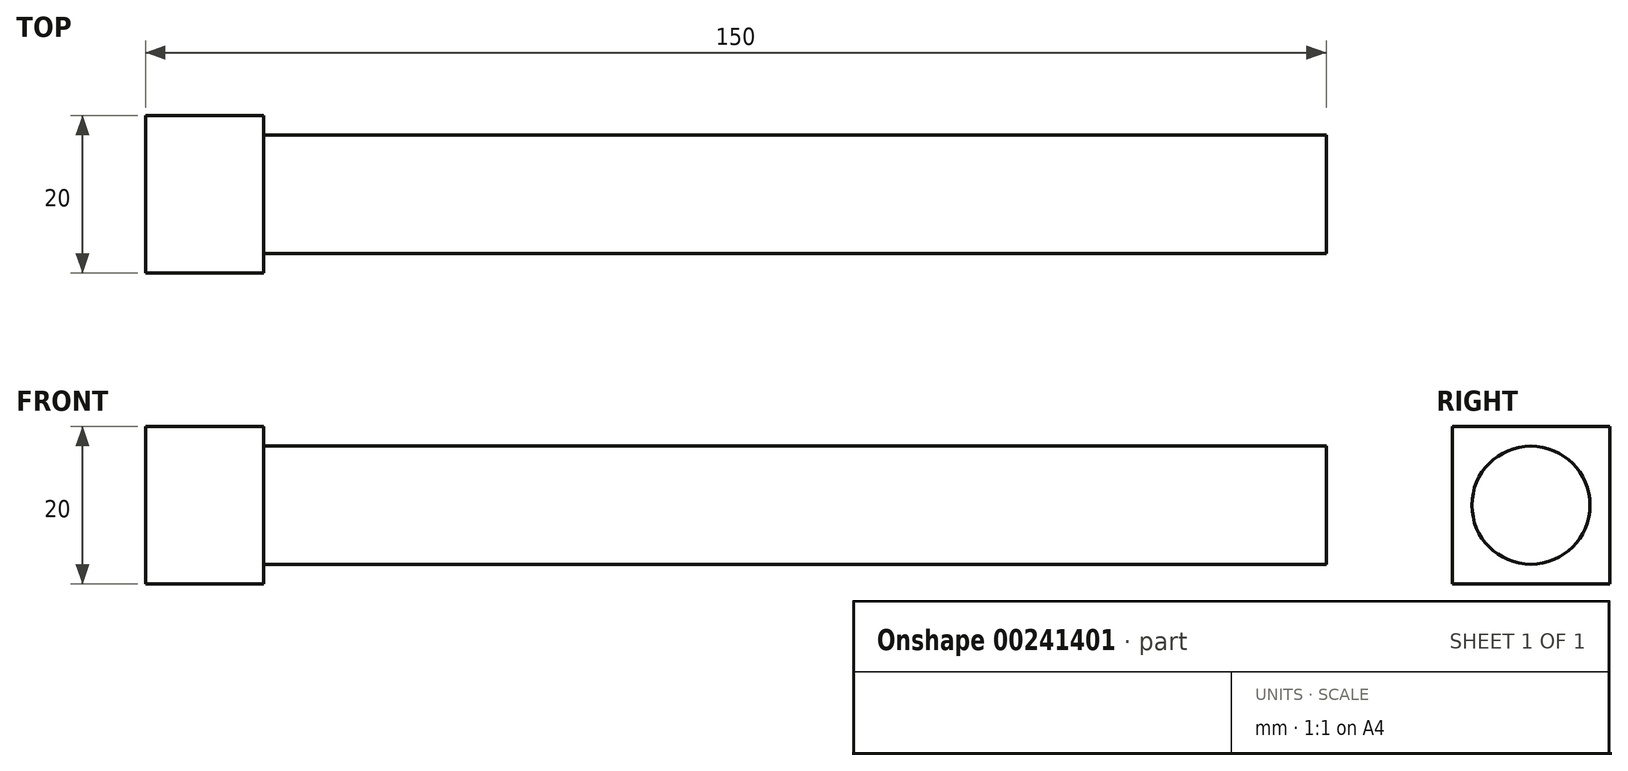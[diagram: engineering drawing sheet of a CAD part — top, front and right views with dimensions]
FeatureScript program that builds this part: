
annotation { "Feature Type Name" : "Feature", "Feature Type Description" : "" }
export const myFeature = defineFeature(function(context is Context, id is Id, definition is map)
    precondition{}
    {
        {
            var Q0;
            Q0=qCreatedBy(makeId("Right.planeOp"),FACE);
            var sketch = newSketch(context, id + "F0", { "sketchPlane" : qUnion([Q0])});
            skLineSegment(sketch, "E0.bottom", {"start": v(-10, 10) * mm, "end": v(10, 10) * mm});
            skLineSegment(sketch, "E0.top", {"start": v(-10, -10) * mm, "end": v(10, -10) * mm});
            skLineSegment(sketch, "E0.left", {"start": v(-10, 10) * mm, "end": v(-10, -10) * mm});
            skLineSegment(sketch, "E0.right", {"start": v(10, 10) * mm, "end": v(10, -10) * mm});
            skPoint(sketch, "E0.middle", {"position": v(0, 0) * mm});
            skSolve(sketch);
        }
        {
            var Q0;
            Q0 = qSketchRegion(id + "F0", true);
            extrude(context, id + "F1", {"entities" : qUnion([Q0]), "depth" : 15 * mm});
        }
        {
            var Q0;
            Q0=makeQuery(id+"F1.opExtrude","CAP_FACE",FACE,{"disambiguationData":[OSD([sQuery(id+"F0.wireOp",EDGE,"E0.bottom"),sQuery(id+"F0.wireOp",EDGE,"E0.top"),sQuery(id+"F0.wireOp",EDGE,"E0.left"),sQuery(id+"F0.wireOp",EDGE,"E0.right")])],"isStart":false});
            var sketch = newSketch(context, id + "F2", { "sketchPlane" : qUnion([Q0])});
            skCircle(sketch, "E1", {"center": v(0, 0) * mm, "radius": 7.5 * mm});
            skSolve(sketch);
        }
        {
            var Q0;
            Q0 = qSketchRegion(id + "F2", true);
            extrude(context, id + "F3", {"entities" : qUnion([Q0]), "operationType" : NewBodyOperationType.ADD, "depth" : 135 * mm});
        }
    });
